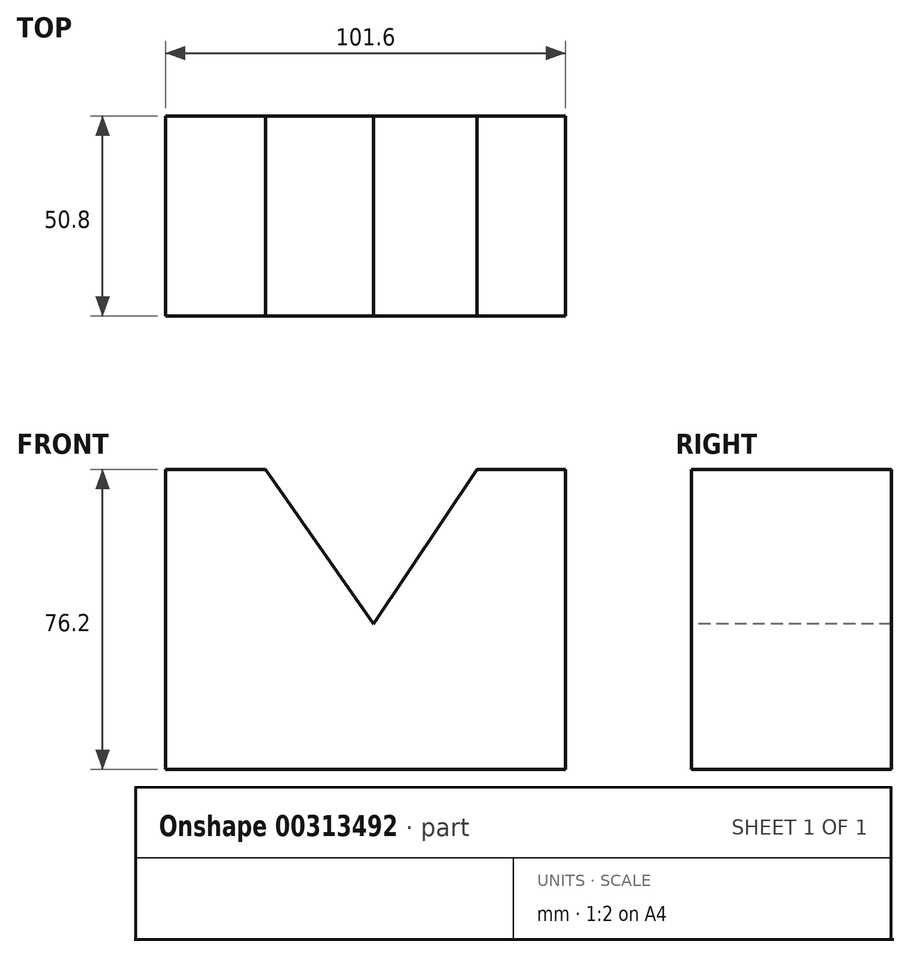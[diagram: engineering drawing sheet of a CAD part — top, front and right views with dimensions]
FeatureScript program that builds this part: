
annotation { "Feature Type Name" : "Feature", "Feature Type Description" : "" }
export const myFeature = defineFeature(function(context is Context, id is Id, definition is map)
    precondition{}
    {
        {
            var Q0;
            Q0=qCreatedBy(makeId("Front.planeOp"),FACE);
            var sketch = newSketch(context, id + "F0", { "sketchPlane" : qUnion([Q0])});
            skLineSegment(sketch, "E0", {"start": v(-52.83, -58) * mm, "end": v(48.77, -58) * mm});
            skLineSegment(sketch, "E1", {"start": v(48.77, -58) * mm, "end": v(48.77, 18.2) * mm});
            skLineSegment(sketch, "E2", {"start": v(48.77, 18.2) * mm, "end": v(23.37, 18.2) * mm});
            skLineSegment(sketch, "E3", {"start": v(-52.83, -58) * mm, "end": v(-52.83, 18.2) * mm});
            skLineSegment(sketch, "E4", {"start": v(-52.83, 18.2) * mm, "end": v(-27.43, 18.2) * mm});
            skLineSegment(sketch, "E5", {"start": v(-27.43, 18.2) * mm, "end": v(0, -21.02) * mm});
            skLineSegment(sketch, "E6", {"start": v(0, -21.02) * mm, "end": v(26.28, 18.2) * mm});
            skSolve(sketch);
        }
        {
            var Q0;
            Q0 = qSketchRegion(id + "F0", true);
            extrude(context, id + "F1", {"entities" : qUnion([Q0]), "oppositeDirection" : true, "depth" : 50.8 * mm});
        }
    });
